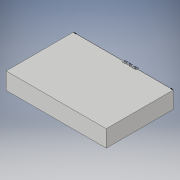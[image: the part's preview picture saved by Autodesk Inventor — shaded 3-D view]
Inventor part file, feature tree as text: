
AUTODESK INVENTOR PART (.ipt)
format: ipt  version: 2018 (Build 220112000, 112)  size: 95,232 bytes
history: native  units: in
note: dims shown in document units (in); Inventor stores cm internally (conversion verified against a paired STEP export)
features: other x2, extrude x1, sketch x1
ambient origin geometry x8: Origin, YZ Plane, XZ Plane, XY Plane, X Axis, Y Axis, Z Axis, Center Point
bodies: Solid1 (feature_tree)
feature tree (4):
  other  "Annotations"
  extrude  "Extrusion1"  Depth=2400.0in
  sketch  "Sketch2"  dims[d2=3576.0in d3=2400.0in d4=600.0in d5=0.0in d6=0.3634in d7=0.0331in d8=3576.0in]
  other  "Linear Dimension 1"
